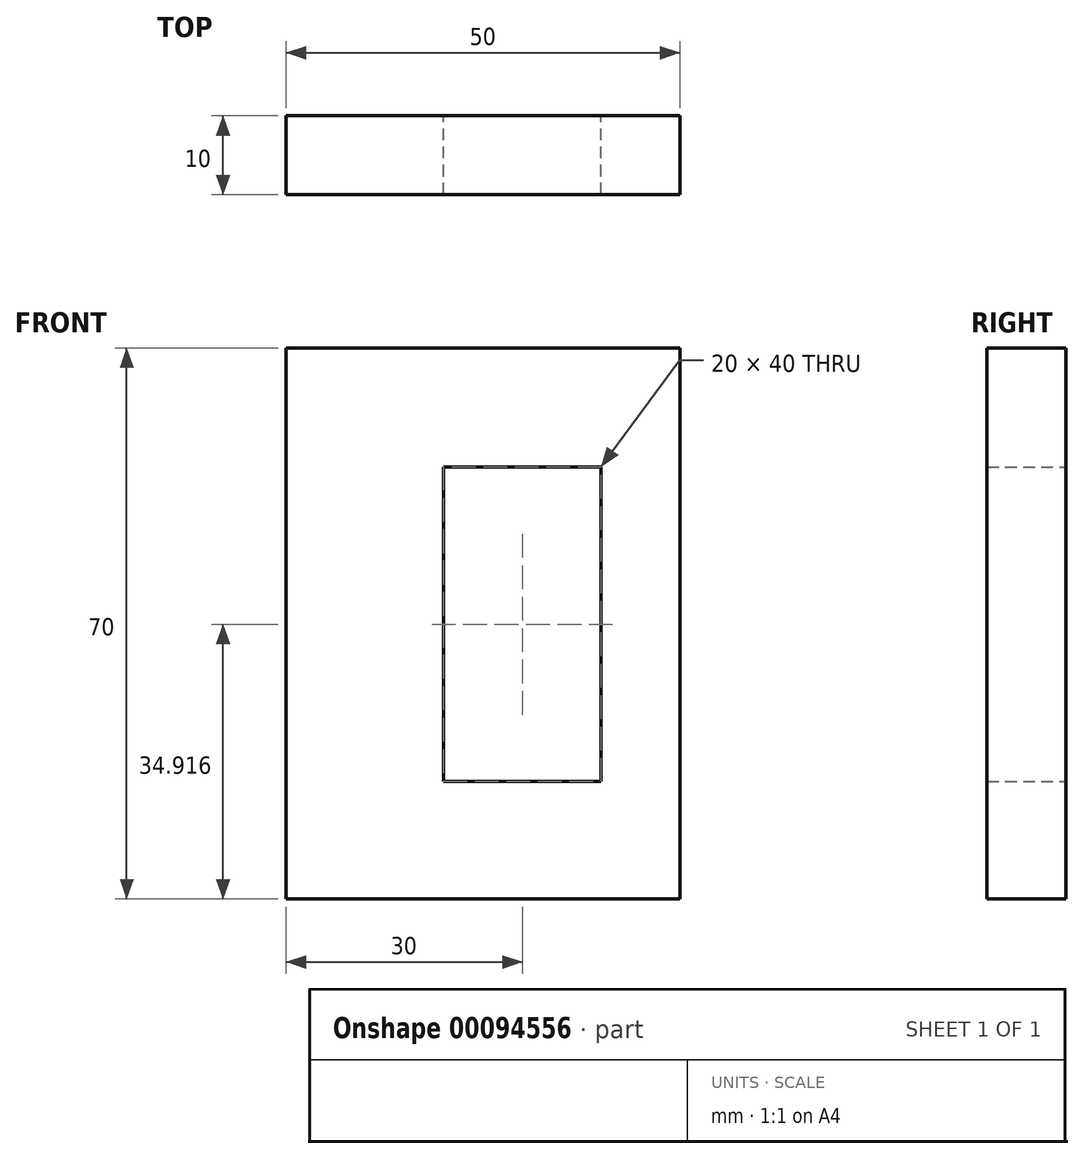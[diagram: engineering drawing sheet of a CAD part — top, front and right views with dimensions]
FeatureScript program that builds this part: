
annotation { "Feature Type Name" : "Feature", "Feature Type Description" : "" }
export const myFeature = defineFeature(function(context is Context, id is Id, definition is map)
    precondition{}
    {
        {
            var Q0;
            Q0=qCreatedBy(makeId("Front.planeOp"),FACE);
            var sketch = newSketch(context, id + "F0", { "sketchPlane" : qUnion([Q0])});
            skLineSegment(sketch, "E0.bottom", {"start": v(0, 0) * mm, "end": v(50, 0) * mm});
            skLineSegment(sketch, "E0.top", {"start": v(0, -70) * mm, "end": v(50, -70) * mm});
            skLineSegment(sketch, "E0.left", {"start": v(0, 0) * mm, "end": v(0, -70) * mm});
            skLineSegment(sketch, "E0.right", {"start": v(50, 0) * mm, "end": v(50, -70) * mm});
            skLineSegment(sketch, "E1.bottom", {"start": v(20, -15.08) * mm, "end": v(40, -15.08) * mm});
            skLineSegment(sketch, "E1.top", {"start": v(20, -55.08) * mm, "end": v(40, -55.08) * mm});
            skLineSegment(sketch, "E1.left", {"start": v(20, -15.08) * mm, "end": v(20, -55.08) * mm});
            skLineSegment(sketch, "E1.right", {"start": v(40, -15.08) * mm, "end": v(40, -55.08) * mm});
            skSolve(sketch);
        }
        {
            var Q0;
            Q0 = qSketchRegion(id + "F0", true);
            extrude(context, id + "F1", {"entities" : qUnion([Q0]), "depth" : 10 * mm});
        }
    });
